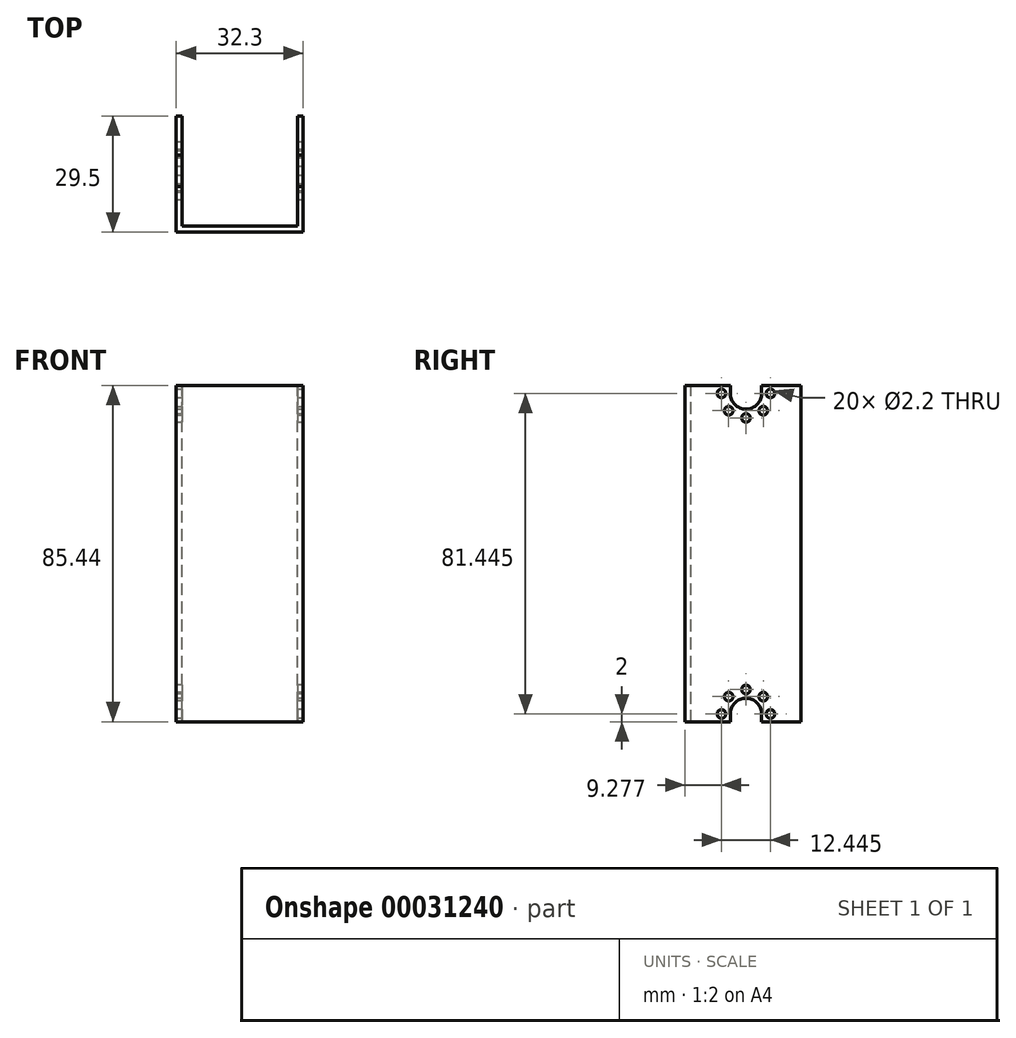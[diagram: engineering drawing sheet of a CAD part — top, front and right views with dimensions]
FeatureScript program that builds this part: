
annotation { "Feature Type Name" : "Feature", "Feature Type Description" : "" }
export const myFeature = defineFeature(function(context is Context, id is Id, definition is map)
    precondition{}
    {
        {
            var Q0;
            Q0=qCreatedBy(makeId("Front.planeOp"),FACE);
            var sketch = newSketch(context, id + "F0", { "sketchPlane" : qUnion([Q0])});
            skLineSegment(sketch, "E0.bottom", {"start": v(0, 0) * mm, "end": v(1.5, 0) * mm});
            skLineSegment(sketch, "E0.top", {"start": v(0, 86.95) * mm, "end": v(32.3, 86.95) * mm});
            skLineSegment(sketch, "E0.left", {"start": v(0, 0) * mm, "end": v(0, 86.95) * mm});
            skLineSegment(sketch, "E0.right", {"start": v(32.3, 0) * mm, "end": v(32.3, 86.95) * mm});
            skLineSegment(sketch, "E1.top", {"start": v(1.5, 85.45) * mm, "end": v(30.8, 85.45) * mm});
            skLineSegment(sketch, "E1.left", {"start": v(1.5, 0) * mm, "end": v(1.5, 85.45) * mm});
            skLineSegment(sketch, "E1.right", {"start": v(30.8, 0) * mm, "end": v(30.8, 85.45) * mm});
            skLineSegment(sketch, "E2.trimOffspring", {"start": v(30.8, 0) * mm, "end": v(32.3, 0) * mm});
            skSolve(sketch);
        }
        {
            var Q0;
            Q0=qSketchRegion(id+"F0",true);
            extrude(context, id + "F1", {"entities" : qUnion([Q0]), "depth" : 28 * mm});
        }
        {
            var Q0;
            Q0=makeQuery(id+"F1.opExtrude","SWEPT_FACE",FACE,{"disambiguationData":[OSD([sQuery(id+"F0.wireOp",EDGE,"E0.left")])]});
            var sketch = newSketch(context, id + "F2", { "sketchPlane" : qUnion([Q0])});
            skArc(sketch, "E3", {"start": v(18, 2) * mm, "mid": v(14, 6) * mm, "end": v(10, 2) * mm});
            skCircle(sketch, "E4", {"center": v(20.22, 2) * mm, "radius": 1.1 * mm});
            skCircle(sketch, "E5.1.0", {"center": v(18.4, 6.4) * mm, "radius": 1.1 * mm});
            skCircle(sketch, "E5.2.0", {"center": v(14, 8.22) * mm, "radius": 1.1 * mm});
            skCircle(sketch, "E5.3.0", {"center": v(9.6, 6.4) * mm, "radius": 1.1 * mm});
            skCircle(sketch, "E5.4.0", {"center": v(7.78, 2) * mm, "radius": 1.1 * mm});
            skLineSegment(sketch, "E6", {"start": v(10, 2) * mm, "end": v(10, 0) * mm});
            skLineSegment(sketch, "E7", {"start": v(18, 2) * mm, "end": v(18, 0) * mm});
            skLineSegment(sketch, "E8", {"start": v(10, 0) * mm, "end": v(18, 0) * mm});
            skLineSegment(sketch, "E9", {"start": v(14, 86.95) * mm, "end": v(14, 0) * mm, "construction": true});
            skPoint(sketch, "E10", {"position": v(14, 0) * mm});
            skLineSegment(sketch, "E11", {"start": v(2.78, 0) * mm, "end": v(0, 0) * mm});
            skLineSegment(sketch, "E12", {"start": v(0, 0) * mm, "end": v(0, 85.45) * mm});
            skLineSegment(sketch, "E13.MirrorCS", {"start": v(28, 0) * mm, "end": v(28, 85.45) * mm});
            skLineSegment(sketch, "E14.MirrorCS", {"start": v(25.22, 0) * mm, "end": v(28, 0) * mm});
            skPoint(sketch, "E15.MirrorCS.end.orphan", {"position": v(28, 85.45) * mm});
            skPoint(sketch, "E15.MirrorCS.start.orphan", {"position": v(25.22, 0) * mm});
            skSolve(sketch);
        }
        {
            var Q0;
            Q0=qSketchRegion(id+"F2",true);
            extrude(context, id + "F3", {"entities" : qUnion([Q0]), "operationType" : NewBodyOperationType.REMOVE, "endBound" : BoundingType.THROUGH_ALL, "oppositeDirection" : true, "depth" : 25 * mm});
        }
        {
            var Q0;
            Q0=makeQuery(id+"F1.opExtrude","SWEPT_FACE",FACE,{"disambiguationData":[OSD([sQuery(id+"F0.wireOp",EDGE,"E0.top")])]});
            var sketch = newSketch(context, id + "F4", { "sketchPlane" : qUnion([Q0])});
            skLineSegment(sketch, "E16", {"start": v(16.15, 0) * mm, "end": v(16.15, -28) * mm, "construction": true});
            skLineSegment(sketch, "E17", {"start": v(0, -14) * mm, "end": v(32.3, -14) * mm, "construction": true});
            skCircle(sketch, "E18", {"center": v(6.15, -4) * mm, "radius": 1.1 * mm});
            skCircle(sketch, "E19.MirrorC", {"center": v(26.15, -4) * mm, "radius": 1.1 * mm});
            skCircle(sketch, "E20.MirrorC", {"center": v(6.15, -24) * mm, "radius": 1.1 * mm});
            skCircle(sketch, "E21.MirrorC", {"center": v(26.15, -24) * mm, "radius": 1.1 * mm});
            skSolve(sketch);
        }
        {
            var Q0;
            Q0=qSketchRegion(id+"F4",true);
            extrude(context, id + "F5", {"entities" : qUnion([Q0]), "operationType" : NewBodyOperationType.REMOVE, "endBound" : BoundingType.UP_TO_NEXT, "oppositeDirection" : true, "depth" : 25 * mm});
        }
        {
            var Q0;
            Q0=makeQuery(id+"F1.opExtrude","SWEPT_FACE",FACE,{"disambiguationData":[OSD([sQuery(id+"F0.wireOp",EDGE,"E0.right")])]});
            var sketch = newSketch(context, id + "F6", { "sketchPlane" : qUnion([Q0])});
            skLineSegment(sketch, "E22.bottom", {"start": v(-28, 86.95) * mm, "end": v(-29.5, 86.95) * mm});
            skLineSegment(sketch, "E22.top", {"start": v(-28, 0) * mm, "end": v(-29.5, 0) * mm});
            skLineSegment(sketch, "E22.left", {"start": v(-28, 86.95) * mm, "end": v(-28, 0) * mm});
            skLineSegment(sketch, "E22.right", {"start": v(-29.5, 86.95) * mm, "end": v(-29.5, 0) * mm});
            skLineSegment(sketch, "E23", {"start": v(-14, 86.95) * mm, "end": v(-14, 0) * mm, "construction": true});
            skLineSegment(sketch, "E24.MirrorCS", {"start": v(0, 86.95) * mm, "end": v(0, 0) * mm});
            skLineSegment(sketch, "E25.MirrorCS", {"start": v(1.5, 86.95) * mm, "end": v(1.5, 0) * mm});
            skLineSegment(sketch, "E26.MirrorCS", {"start": v(0, 86.95) * mm, "end": v(1.5, 86.95) * mm});
            skLineSegment(sketch, "E27.MirrorCS", {"start": v(0, 0) * mm, "end": v(1.5, 0) * mm});
            skSolve(sketch);
        }
        {
            var Q0;
            Q0=makeQuery(id+"F6.imprint","IMPRINT",FACE,{"disambiguationData":[TD([[makeQuery(id+"F6.imprint","IMPRINT",EDGE,{"derivedFrom":sQuery(id+"F6.wireOp",EDGE,"E22.bottom")}),1.0]])]});
            extrude(context, id + "F7", {"entities" : qUnion([Q0]), "operationType" : NewBodyOperationType.ADD, "oppositeDirection" : true, "depth" : 32.3 * mm});
        }
        {
            var Q0;
            Q0=makeQuery(id+"F7.boolean.opBoolean","MERGE",FACE,{"derivedFrom":[makeQuery(id+"F1.opExtrude","SWEPT_FACE",FACE,{"disambiguationData":[OSD([sQuery(id+"F0.wireOp",EDGE,"E0.right")])]}),makeQuery(id+"F7.opExtrude","CAP_FACE",FACE,{"disambiguationData":[OSD([sQuery(id+"F6.wireOp",EDGE,"E22.bottom"),sQuery(id+"F6.wireOp",EDGE,"E22.top"),sQuery(id+"F6.wireOp",EDGE,"E22.left"),sQuery(id+"F6.wireOp",EDGE,"E22.right")])],"isStart":true})]});
            var sketch = newSketch(context, id + "F8", { "sketchPlane" : qUnion([Q0])});
            skLineSegment(sketch, "E28.bottom", {"start": v(-29.5, 86.95) * mm, "end": v(0, 86.95) * mm});
            skLineSegment(sketch, "E28.top", {"start": v(-29.5, 85.45) * mm, "end": v(0, 85.45) * mm});
            skLineSegment(sketch, "E28.left", {"start": v(-29.5, 86.95) * mm, "end": v(-29.5, 85.45) * mm});
            skLineSegment(sketch, "E28.right", {"start": v(0, 86.95) * mm, "end": v(0, 85.45) * mm});
            skLineSegment(sketch, "E29", {"start": v(-29.5, 42.72) * mm, "end": v(0, 42.72) * mm, "construction": true});
            skCircle(sketch, "E30.0", {"center": v(-18.4, 6.4) * mm, "radius": 1.1 * mm});
            skCircle(sketch, "E30.1", {"center": v(-14, 8.22) * mm, "radius": 1.1 * mm});
            skCircle(sketch, "E30.2", {"center": v(-9.6, 6.4) * mm, "radius": 1.1 * mm});
            skArc(sketch, "E30.3", {"start": v(-18, 2) * mm, "mid": v(-14, 6) * mm, "end": v(-10, 2) * mm});
            skCircle(sketch, "E30.4", {"center": v(-7.78, 2) * mm, "radius": 1.1 * mm});
            skCircle(sketch, "E30.5", {"center": v(-20.22, 2) * mm, "radius": 1.1 * mm});
            skLineSegment(sketch, "E30.6", {"start": v(-18, 2) * mm, "end": v(-18, 0) * mm});
            skCircle(sketch, "E30.7", {"center": v(-20.22, 2) * mm, "radius": 1.1 * mm});
            skLineSegment(sketch, "E30.8", {"start": v(-10, 2) * mm, "end": v(-10, 0) * mm});
            skCircle(sketch, "E30.9", {"center": v(-7.78, 2) * mm, "radius": 1.1 * mm});
            skCircle(sketch, "E30.10", {"center": v(-18.4, 6.4) * mm, "radius": 1.1 * mm});
            skArc(sketch, "E30.13", {"start": v(-18, 2) * mm, "mid": v(-14, 6) * mm, "end": v(-10, 2) * mm});
            skCircle(sketch, "E30.14", {"center": v(-14, 8.22) * mm, "radius": 1.1 * mm});
            skCircle(sketch, "E30.15", {"center": v(-20.22, 2) * mm, "radius": 1.1 * mm});
            skLineSegment(sketch, "E30.16", {"start": v(-10, 2) * mm, "end": v(-10, 0) * mm});
            skCircle(sketch, "E30.17", {"center": v(-9.6, 6.4) * mm, "radius": 1.1 * mm});
            skLineSegment(sketch, "E30.20", {"start": v(-18, 2) * mm, "end": v(-18, 0) * mm});
            skCircle(sketch, "E30.21", {"center": v(-14, 8.22) * mm, "radius": 1.1 * mm});
            skArc(sketch, "E30.22", {"start": v(-18, 2) * mm, "mid": v(-14, 6) * mm, "end": v(-10, 2) * mm});
            skCircle(sketch, "E30.23", {"center": v(-9.6, 6.4) * mm, "radius": 1.1 * mm});
            skCircle(sketch, "E30.24", {"center": v(-20.22, 2) * mm, "radius": 1.1 * mm});
            skLineSegment(sketch, "E30.25", {"start": v(-10, 2) * mm, "end": v(-10, 0) * mm});
            skCircle(sketch, "E30.26", {"center": v(-18.4, 6.4) * mm, "radius": 1.1 * mm});
            skCircle(sketch, "E30.27", {"center": v(-7.78, 2) * mm, "radius": 1.1 * mm});
            skLineSegment(sketch, "E30.29", {"start": v(-10, 2) * mm, "end": v(-10, 0) * mm});
            skLineSegment(sketch, "E30.31", {"start": v(-18, 2) * mm, "end": v(-18, 0) * mm});
            skArc(sketch, "E30.33", {"start": v(-18, 2) * mm, "mid": v(-14, 6) * mm, "end": v(-10, 2) * mm});
            skCircle(sketch, "E30.35", {"center": v(-18.4, 6.4) * mm, "radius": 1.1 * mm});
            skCircle(sketch, "E30.36", {"center": v(-14, 8.22) * mm, "radius": 1.1 * mm});
            skCircle(sketch, "E30.37", {"center": v(-9.6, 6.4) * mm, "radius": 1.1 * mm});
            skCircle(sketch, "E30.38", {"center": v(-7.78, 2) * mm, "radius": 1.1 * mm});
            skLineSegment(sketch, "E30.39", {"start": v(-18, 2) * mm, "end": v(-18, 0) * mm});
            skLineSegment(sketch, "E31.MirrorCS", {"start": v(-10, 83.44) * mm, "end": v(-10, 85.44) * mm});
            skLineSegment(sketch, "E32.MirrorCS", {"start": v(-18, 83.44) * mm, "end": v(-18, 85.44) * mm});
            skCircle(sketch, "E33.MirrorC", {"center": v(-9.6, 79.05) * mm, "radius": 1.1 * mm});
            skCircle(sketch, "E34.MirrorC", {"center": v(-18.4, 79.04) * mm, "radius": 1.1 * mm});
            skCircle(sketch, "E35.MirrorC", {"center": v(-7.78, 83.45) * mm, "radius": 1.1 * mm});
            skCircle(sketch, "E36.MirrorC", {"center": v(-14, 77.22) * mm, "radius": 1.1 * mm});
            skCircle(sketch, "E37.MirrorC", {"center": v(-20.22, 83.44) * mm, "radius": 1.1 * mm});
            skArc(sketch, "E38.MirrorCS", {"start": v(-18, 83.44) * mm, "mid": v(-14, 79.44) * mm, "end": v(-10, 83.44) * mm});
            skSolve(sketch);
        }
        {
            var Q0;
            Q0 = qSketchRegion(id + "F8", true);
            extrude(context, id + "F9", {"entities" : qUnion([Q0]), "operationType" : NewBodyOperationType.REMOVE, "endBound" : BoundingType.THROUGH_ALL, "oppositeDirection" : true, "depth" : 25 * mm});
        }
    });
